# Revit family: Wood_Lockers-Salsbury_Industries-22000_Series-1_Wide_Units
name_source: partatom
category: Specialty Equipment
revit_build: Autodesk Revit 2016 (Build: 20150714_1515(x64)
units: mm (PartAtom-declared; Revit-internal decimal feet)

## family parameters
Always vertical = Yes
Cut with Voids When Loaded = No
OmniClass Number = 23.40.00.00
OmniClass Title = Equipment and Furnishings
Part Type = Normal
Room Calculation Point = No
Round Connector Dimension = Use Diameter
Shared = No
Work Plane-Based = No

## types (6) — shared parameters
Assembly Code = C1030310
Door Location D1 = Wood Locker Doors : Extra Wide Double Tier Door
Door Trim = Rubber Trim - Salsbury Finish - Textured
Hardware = Aluminum - Salsbury Finish - Black Satin
Individual Door Height = 35.781"
Manufacturer = Salsbury Industries
MasterFormat Code = 10 51 23
MasterFormat Title = Lockers
OmniClass 23 Number = 23.40.00.00
OmniClass 23 Title = Equipment and Furnishings
Primary Structure Materials = Particle Board Industrial Grade - Salsbury Finish - White Melamine Inlay
Secondary Structure Materials = Particle Board Industrial Grade - Salsbury Finish - Black Melamine Overlay
Type Comments = 15" Wide Designer Wood Lockers - Double Tier
URL = www.lockers.com
Unit Height = 72.000"
Unit Trim = Melamine - Salsbury Finish - Black
Version = 2.0 (04/30/18)
Width = 15.000"

## per-type parameters (varying)
| type | Base | Base Height | Depth | Description | Model | Sloping Hood Height |
| 22164 | Wood Locker Bases : Base - 15" W x 24" D Lockers | 4.000" | 24.000" | 1 Wide - 6 Feet High - 24 inches Deep - with Base | 22164 | 9.118" |
| 22164 - without Base | Wood Locker Bases : None | 0.000" | 24.000" | 1 Wide - 6 Feet High - 24 inches Deep - without Base | 22164 without Base | 9.118" |
| 22168 | Wood Locker Bases : Base - 15" W x 18" D Lockers | 4.000" | 18.000" | 1 Wide - 6 Feet High - 18 inches Deep - with Base | 22168 | 6.868" |
| 22168 - without Base | Wood Locker Bases : None | 0.000" | 18.000" | 1 Wide - 6 Feet High - 18 inches Deep - without Base | 22168 without Base | 6.868" |
| 22161 | Wood Locker Bases : Base - 15" W x 21" D Lockers | 4.000" | 21.000" | 1 Wide - 6 Feet High - 21 inches Deep - with Base | 22161 | 7.993" |
| 22161 - without Base | Wood Locker Bases : None | 0.000" | 21.000" | 1 Wide - 6 Feet High - 21 inches Deep - without Base | 22161 without Base | 7.993" |

## geometry (parser evidence)
native form markers: Sweep x32
no freeform markers — native parametric forms only
